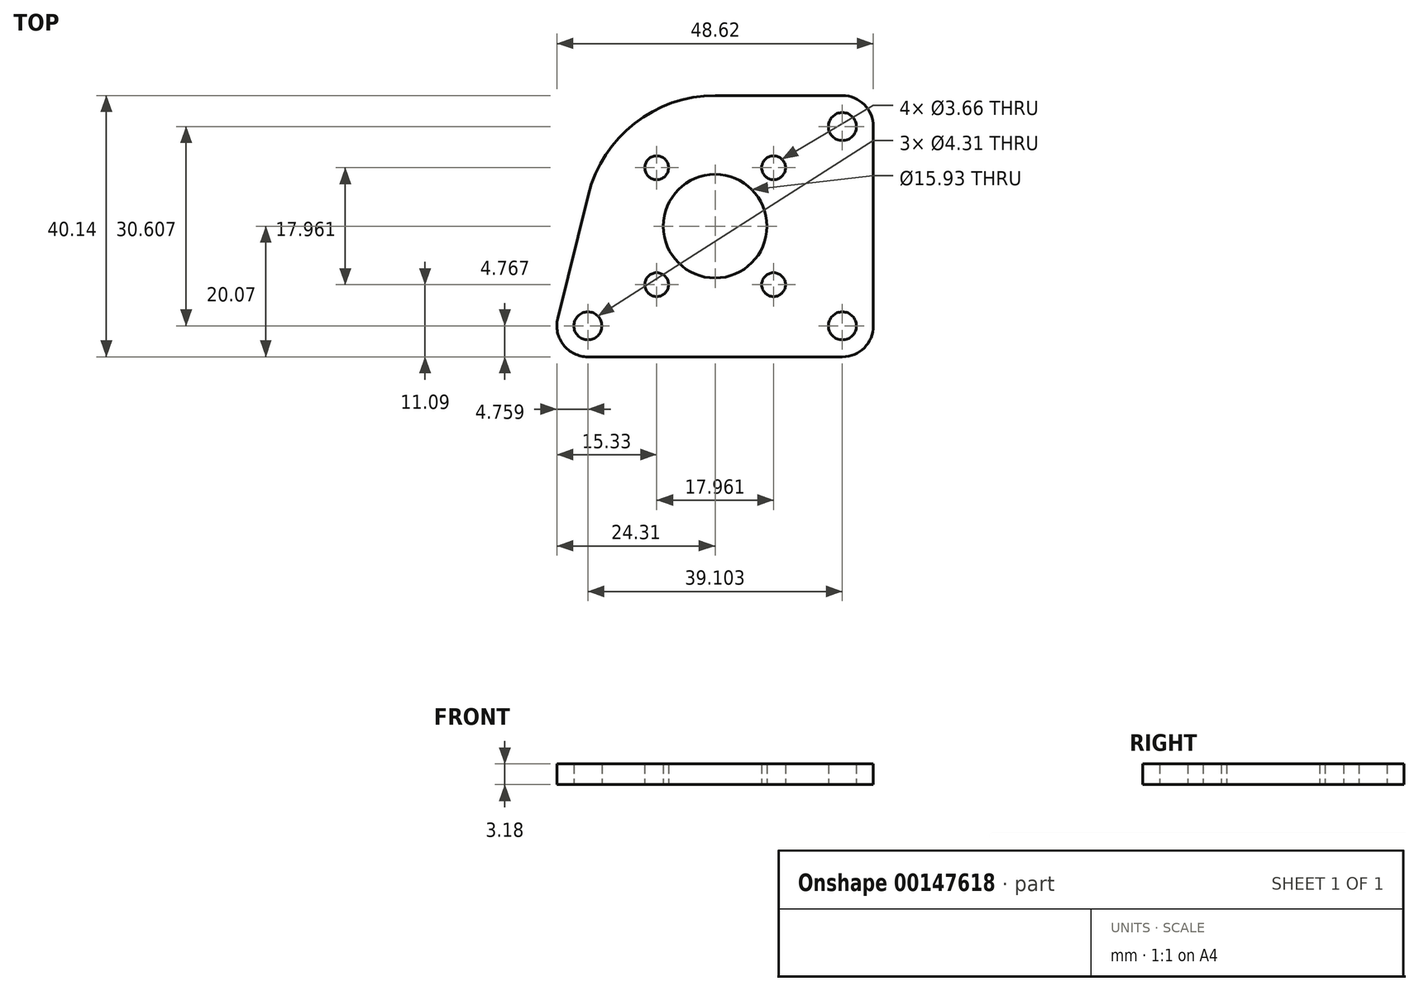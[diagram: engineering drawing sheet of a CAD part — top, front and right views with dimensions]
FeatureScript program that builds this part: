
annotation { "Feature Type Name" : "Feature", "Feature Type Description" : "" }
export const myFeature = defineFeature(function(context is Context, id is Id, definition is map)
    precondition{}
    {
        {
            var Q0;
            Q0=qCreatedBy(makeId("Top.planeOp"),FACE);
            var sketch = newSketch(context, id + "F0", { "sketchPlane" : qUnion([Q0])});
            skCircle(sketch, "E0", {"center": v(-19.55, -15.3) * mm, "radius": 2.15 * mm});
            skArc(sketch, "E1", {"start": v(0, 20.07) * mm, "mid": v(-12.37, 15.8) * mm, "end": v(-19.48, 4.82) * mm});
            skArc(sketch, "E2", {"start": v(-24.17, -14.16) * mm, "mid": v(-23.3, -18.24) * mm, "end": v(-19.55, -20.07) * mm});
            skArc(sketch, "E3", {"start": v(-19.48, 4.82) * mm, "mid": v(12.37, -15.8) * mm, "end": v(0, 20.07) * mm, "construction": true});
            skArc(sketch, "E4", {"start": v(-19.55, -20.07) * mm, "mid": v(-15.8, -12.37) * mm, "end": v(-24.17, -14.16) * mm, "construction": true});
            skLineSegment(sketch, "E5", {"start": v(-19.48, 4.82) * mm, "end": v(-24.17, -14.16) * mm});
            skLineSegment(sketch, "E6", {"start": v(-19.55, -20.07) * mm, "end": v(19.55, -20.07) * mm});
            skLineSegment(sketch, "E7", {"start": v(0, 20.07) * mm, "end": v(19.55, 20.07) * mm});
            skArc(sketch, "E8", {"start": v(19.55, -20.07) * mm, "mid": v(22.92, -18.67) * mm, "end": v(24.31, -15.3) * mm});
            skArc(sketch, "E9", {"start": v(24.31, -15.3) * mm, "mid": v(16.18, -11.94) * mm, "end": v(19.55, -20.07) * mm, "construction": true});
            skArc(sketch, "E10", {"start": v(19.55, 20.07) * mm, "mid": v(16.18, 11.94) * mm, "end": v(24.31, 15.3) * mm, "construction": true});
            skLineSegment(sketch, "E11", {"start": v(24.31, -15.3) * mm, "end": v(24.31, 15.3) * mm});
            skArc(sketch, "E12", {"start": v(24.31, 15.3) * mm, "mid": v(22.92, 18.67) * mm, "end": v(19.55, 20.07) * mm});
            skCircle(sketch, "E13", {"center": v(19.55, -15.3) * mm, "radius": 2.15 * mm});
            skCircle(sketch, "E14", {"center": v(19.55, 15.3) * mm, "radius": 2.15 * mm});
            skLineSegment(sketch, "E15.bottom", {"start": v(8.98, 8.98) * mm, "end": v(-8.98, 8.98) * mm, "construction": true});
            skLineSegment(sketch, "E15.top", {"start": v(8.98, -8.98) * mm, "end": v(-8.98, -8.98) * mm, "construction": true});
            skLineSegment(sketch, "E15.left", {"start": v(8.98, 8.98) * mm, "end": v(8.98, -8.98) * mm, "construction": true});
            skLineSegment(sketch, "E15.right", {"start": v(-8.98, 8.98) * mm, "end": v(-8.98, -8.98) * mm, "construction": true});
            skLineSegment(sketch, "E16", {"start": v(0, 0) * mm, "end": v(8.98, 8.98) * mm, "construction": true});
            skCircle(sketch, "E17", {"center": v(-8.98, 8.98) * mm, "radius": 1.83 * mm});
            skCircle(sketch, "E18", {"center": v(8.98, 8.98) * mm, "radius": 1.83 * mm});
            skCircle(sketch, "E19", {"center": v(8.98, -8.98) * mm, "radius": 1.83 * mm});
            skCircle(sketch, "E20", {"center": v(-8.98, -8.98) * mm, "radius": 1.83 * mm});
            skCircle(sketch, "E21", {"center": v(0, 0) * mm, "radius": 7.96 * mm});
            skSolve(sketch);
        }
        {
            var Q0;
            Q0=qSketchRegion(id+"F0",true);
            extrude(context, id + "F1", {"entities" : qUnion([Q0]), "depth" : 3.17 * mm});
        }
    });
